# Revit family: VE_Air Heater_MEPcontent_Mark_Ecofan W_INT-EN_v2
name_source: partatom
category: Mechanical Equipment
units: mm (PartAtom-declared; Revit-internal decimal feet)

## family parameters
Always vertical = Yes
Cut with Voids When Loaded = No
Maintain Annotation Orientation = No
OmniClass Number = 23.75.70.17
OmniClass Title = Water Heated and Cooled Terminal Heating and Cooling Units
Part Type = Normal
Room Calculation Point = No
Round Connector Dimension = Use Diameter
Shared = No
Work Plane-Based = No

## types (8) — shared parameters
Air Flow Rate = 0.0 L/s
Article Description = ECOFAN with thermostat and switch
Base Family Version = 24.10
Custom = No
Description = ECOFAN with thermostat and switch
EMCS Version = 5.0
ETIM Article Class = EC011395
Heating Power = 0 W
IFCExportAs = IfcAirTerminal
IFCExportType = NOTDEFINED
MEPcontent Class = AIR_HEATER
Manufacturer = Mark
Manufacturer URL = http://www.markclimate.com
Nominal Flow Rate = 0.0 L/s
Product Line = Mark
Revit Version = 2022
Voltage = 230 V
zero-valued in all types: Default Elevation

## per-type parameters (varying)
| type | Article Type | Carcase Depth | Conus | Distance Between Horizontal Fan Grids | Distance Between Pendants | Distance Vertical Fan Grids | Fan Grid Length | GTIN | Half Width | Height | Length | Manufacturer Art. No. | Model | Power | Radius Fan Grid | URL | W142 | W42 | W82 | Width |
| W42 with thermostat and switch | W42 with thermostat and switch | 153.1 mm  [stored 0.502297 ft] | No | 16 mm  [stored 0.0524934 ft] | 500 mm  [stored 1.64042 ft] | 135 mm  [stored 0.442913 ft] | 71 mm  [stored 0.23294 ft] | 87193336500500 | 280 mm  [stored 0.918635 ft] | 245 mm  [stored 0.803806 ft] | 560 mm  [stored 1.83727 ft] | 5065005 | W42 with thermostat and switch | 150 W | 230 mm  [stored 0.754593 ft] | https://mep.trimble.com | No | Yes | No | 560 mm  [stored 1.83727 ft] |
| W142 EC with thermostat and switch | W142 EC with thermostat and switch | 178.3 mm  [stored 0.584974 ft] | No | 15 mm  [stored 0.0492126 ft] | 797 mm  [stored 2.61483 ft] | 210 mm  [stored 0.688976 ft] | 68 mm | 87193336501408 | 430 mm  [stored 1.41076 ft] | 452 mm  [stored 1.48294 ft] | 860 mm  [stored 2.82152 ft] | 5065014 | W142 EC with thermostat and switch | 535 W | 0 mm  [stored 0 ft] | https://mep.trimble.com | Yes | No | No | 860 mm  [stored 2.82152 ft] |
| W82 EC with thermostat and switch | W82 EC with thermostat and switch | 141.8 mm  [stored 0.465223 ft] | No | 23 mm  [stored 0.0754593 ft] | 600 mm | 145 mm  [stored 0.475722 ft] | 71 mm  [stored 0.23294 ft] | 87193336500807 | 360 mm  [stored 1.1811 ft] | 390 mm  [stored 1.27953 ft] | 720 mm  [stored 2.3622 ft] | 5065008 | W82 EC with thermostat and switch | 360 W | 295 mm  [stored 0.967848 ft] | https://mep.trimble.com | No | No | Yes | 720 mm  [stored 2.3622 ft] |
| W42 EC with thermostat and switch | W42 EC with thermostat and switch | 153.1 mm  [stored 0.502297 ft] | No | 16 mm  [stored 0.0524934 ft] | 500 mm  [stored 1.64042 ft] | 135 mm  [stored 0.442913 ft] | 71 mm  [stored 0.23294 ft] | 87193336500302 | 280 mm  [stored 0.918635 ft] | 245 mm  [stored 0.803806 ft] | 560 mm  [stored 1.83727 ft] | 5065003 | W42 EC with thermostat and switch | 150 W | 230 mm  [stored 0.754593 ft] | https://mep.trimble.com | No | Yes | No | 560 mm  [stored 1.83727 ft] |
| W142 with thermostat and switch | W142 with thermostat and switch | 178.3 mm  [stored 0.584974 ft] | No | 15 mm  [stored 0.0492126 ft] | 797 mm  [stored 2.61483 ft] | 210 mm  [stored 0.688976 ft] | 68 mm | 87193336501200 | 430 mm  [stored 1.41076 ft] | 452 mm  [stored 1.48294 ft] | 860 mm  [stored 2.82152 ft] | 5065012 | W142 with thermostat and switch | 535 W | 0 mm  [stored 0 ft] | https://mep.trimble.com | Yes | No | No | 860 mm  [stored 2.82152 ft] |
| W82 with thermostat and switch | W82 with thermostat and switch | 141.8 mm  [stored 0.465223 ft] | No | 23 mm  [stored 0.0754593 ft] | 600 mm | 145 mm  [stored 0.475722 ft] | 71 mm  [stored 0.23294 ft] | 87193336501002 | 360 mm  [stored 1.1811 ft] | 390 mm  [stored 1.27953 ft] | 720 mm  [stored 2.3622 ft] | 5065010 | W82 with thermostat and switch | 360 W | 295 mm  [stored 0.967848 ft] | https://mep.trimble.com | No | No | Yes | 720 mm  [stored 2.3622 ft] |
| W142 EC with thermostat and switch and conus | W142 with thermostat and switch | 178.3 mm  [stored 0.584974 ft] | Yes | 15 mm  [stored 0.0492126 ft] | 797 mm  [stored 2.61483 ft] | 210 mm  [stored 0.688976 ft] | 68 mm | 87193336501200 | 430 mm  [stored 1.41076 ft] | 452 mm  [stored 1.48294 ft] | 860 mm  [stored 2.82152 ft] | 5065012 | W142 with thermostat and switch | 535 W | 0 mm  [stored 0 ft] | https://mep.trimble.com | Yes | No | No | 860 mm  [stored 2.82152 ft] |
| W142 with thermostat and switch and conus | W142 with thermostat and switch | 178.3 mm  [stored 0.584974 ft] | Yes | 15 mm  [stored 0.0492126 ft] | 797 mm  [stored 2.61483 ft] | 210 mm  [stored 0.688976 ft] | 68 mm | 87193336501200 | 430 mm  [stored 1.41076 ft] | 452 mm  [stored 1.48294 ft] | 860 mm  [stored 2.82152 ft] | 5065012 | W142 with thermostat and switch | 535 W | 0 mm  [stored 0 ft] |  | Yes | No | No | 860 mm  [stored 2.82152 ft] |

note: [stored X ft] marks values corroborated as IEEE doubles in the binary element streams (Revit-internal decimal feet)

## geometry (parser evidence)
native form markers: Sweep x12
no freeform markers — native parametric forms only
